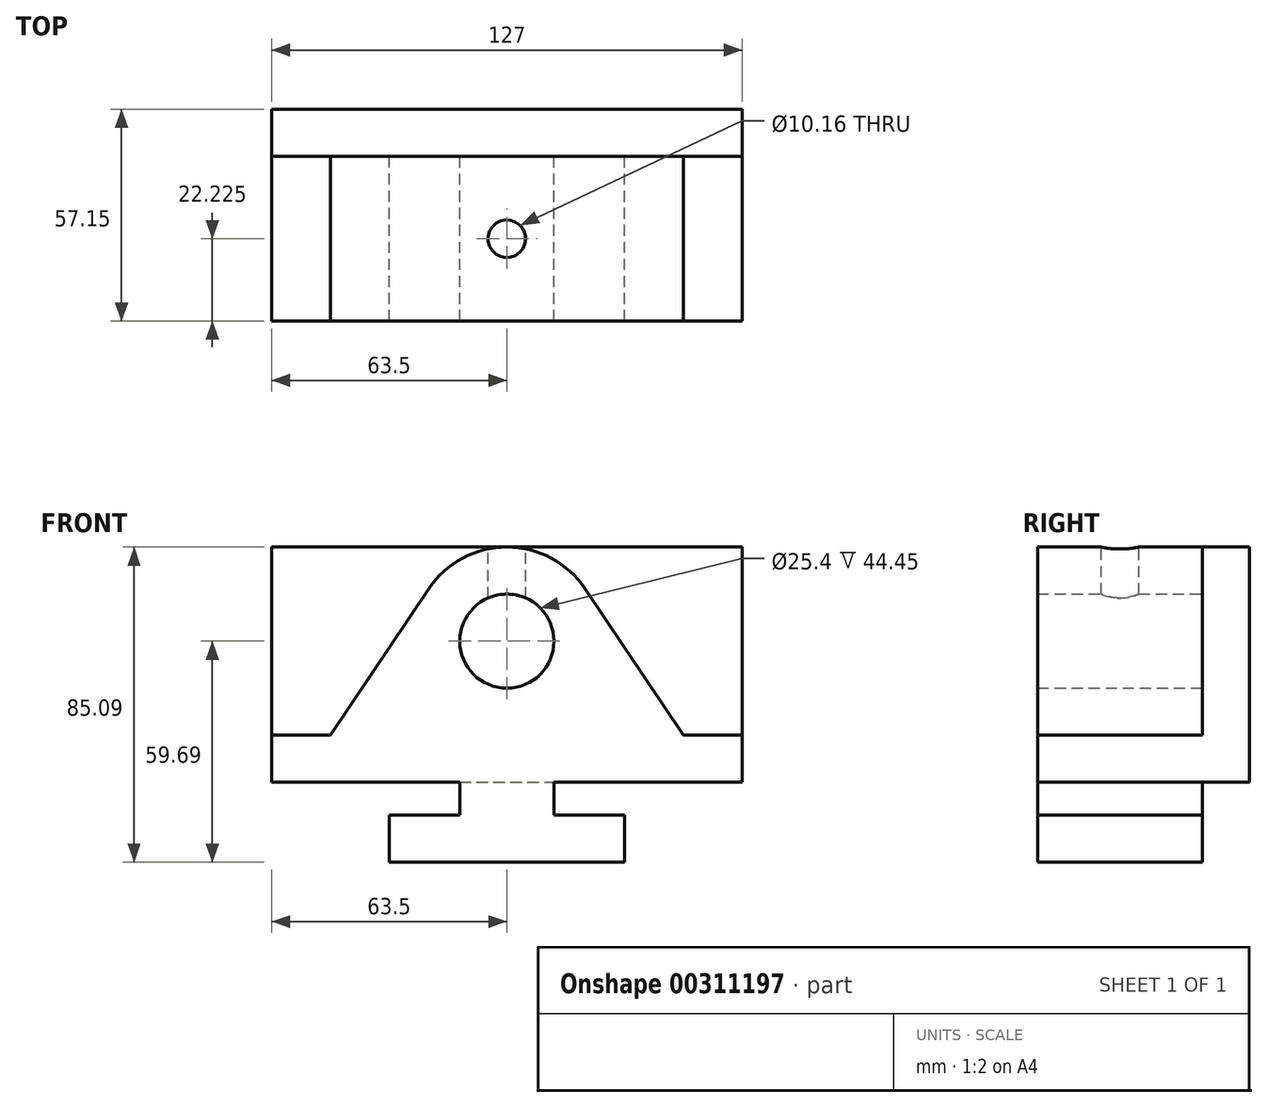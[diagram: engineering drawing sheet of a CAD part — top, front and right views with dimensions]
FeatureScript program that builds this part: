
annotation { "Feature Type Name" : "Feature", "Feature Type Description" : "" }
export const myFeature = defineFeature(function(context is Context, id is Id, definition is map)
    precondition{}
    {
        {
            var Q0;
            Q0=qCreatedBy(makeId("Front.planeOp"),FACE);
            var sketch = newSketch(context, id + "F0", { "sketchPlane" : qUnion([Q0])});
            skLineSegment(sketch, "E0", {"start": v(0, 0) * mm, "end": v(31.75, 0) * mm});
            skLineSegment(sketch, "E1", {"start": v(31.75, 0) * mm, "end": v(31.75, 12.7) * mm});
            skLineSegment(sketch, "E2", {"start": v(31.75, 12.7) * mm, "end": v(12.7, 12.7) * mm});
            skLineSegment(sketch, "E3", {"start": v(0, 0) * mm, "end": v(-31.75, 0) * mm});
            skLineSegment(sketch, "E4", {"start": v(-31.75, 0) * mm, "end": v(-31.75, 12.7) * mm});
            skLineSegment(sketch, "E5", {"start": v(-31.75, 12.7) * mm, "end": v(-12.7, 12.7) * mm});
            skLineSegment(sketch, "E6", {"start": v(-12.7, 12.7) * mm, "end": v(-12.7, 21.6) * mm});
            skLineSegment(sketch, "E7", {"start": v(-12.7, 21.59) * mm, "end": v(-63.5, 21.59) * mm});
            skLineSegment(sketch, "E8", {"start": v(-63.5, 21.6) * mm, "end": v(-63.5, 34.29) * mm});
            skLineSegment(sketch, "E9", {"start": v(-63.5, 34.3) * mm, "end": v(-47.62, 34.3) * mm});
            skLineSegment(sketch, "E10", {"start": v(12.7, 12.7) * mm, "end": v(12.7, 21.6) * mm});
            skLineSegment(sketch, "E11", {"start": v(12.7, 21.59) * mm, "end": v(63.5, 21.59) * mm});
            skLineSegment(sketch, "E12", {"start": v(63.5, 21.6) * mm, "end": v(63.5, 34.3) * mm});
            skLineSegment(sketch, "E13", {"start": v(63.5, 34.3) * mm, "end": v(47.62, 34.3) * mm});
            skLineSegment(sketch, "E14", {"start": v(47.62, 34.3) * mm, "end": v(21.1, 73.84) * mm});
            skLineSegment(sketch, "E15", {"start": v(-47.63, 34.29) * mm, "end": v(-21.1, 73.84) * mm});
            skArc(sketch, "E16", {"start": v(21.1, 73.84) * mm, "mid": v(0, 85.1) * mm, "end": v(-21.1, 73.84) * mm});
            skCircle(sketch, "E17", {"center": v(0, 59.69) * mm, "radius": 12.7 * mm});
            skSolve(sketch);
        }
        {
            var Q0;
            Q0 = qSketchRegion(id + "F0", true);
            extrude(context, id + "F1", {"entities" : qUnion([Q0]), "depth" : 44.45 * mm});
        }
        {
            var Q0;
            Q0=makeQuery(id+"F1.opExtrude","SWEPT_FACE",FACE,{"disambiguationData":[OSD([sQuery(id+"F0.wireOp",EDGE,"E12")])]});
            var sketch = newSketch(context, id + "F2", { "sketchPlane" : qUnion([Q0])});
            skLineSegment(sketch, "E18", {"start": v(0, 21.59) * mm, "end": v(0, 85.1) * mm});
            skLineSegment(sketch, "E19", {"start": v(0, 85.1) * mm, "end": v(12.7, 85.1) * mm});
            skLineSegment(sketch, "E20", {"start": v(12.7, 85.1) * mm, "end": v(12.7, 21.59) * mm});
            skLineSegment(sketch, "E21", {"start": v(12.7, 21.59) * mm, "end": v(0, 21.59) * mm});
            skSolve(sketch);
        }
        {
            var Q0;
            Q0 = qSketchRegion(id + "F2", true);
            extrude(context, id + "F3", {"entities" : qUnion([Q0]), "operationType" : NewBodyOperationType.ADD, "oppositeDirection" : true, "depth" : 127 * mm});
        }
        {
            var Q0;
            Q0=qCreatedBy(makeId("Top.planeOp"),FACE);
            cPlane(context, id + "F4", {"entities" : qUnion([Q0]), "cplaneType" : CPlaneType.OFFSET, "offset" : 85.1 * mm, "width" : 152.4 * mm, "height" : 152.4 * mm});
        }
        {
            var Q0;
            Q0=qCreatedBy(id+"F4.planeOp",FACE);
            var sketch = newSketch(context, id + "F5", { "sketchPlane" : qUnion([Q0])});
            skCircle(sketch, "E22", {"center": v(0, -22.23) * mm, "radius": 5.08 * mm});
            skSolve(sketch);
        }
        {
            var Q0;
            Q0 = qSketchRegion(id + "F5", true);
            extrude(context, id + "F6", {"entities" : qUnion([Q0]), "operationType" : NewBodyOperationType.REMOVE, "oppositeDirection" : true, "depth" : 25.4 * mm});
        }
    });
